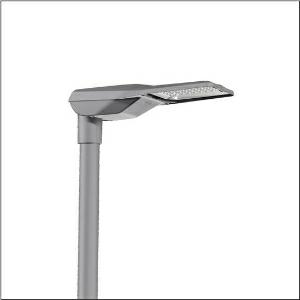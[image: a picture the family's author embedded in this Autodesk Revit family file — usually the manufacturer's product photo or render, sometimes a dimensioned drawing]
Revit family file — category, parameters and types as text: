
# Revit family: streetlight_sl_21_iq_mini___p0_8ab_5xe2r31g08hb_d767
name_source: partatom
category: Lighting Fixtures
units: mm (PartAtom-declared; Revit-internal decimal feet)

## family parameters
Cut with Voids When Loaded = No
Host = Face
Light Source = No
Part Type = Normal
Room Calculation Point = No
Round Connector Dimension = Use Diameter
Shared = No

## types (1)
- --- (1 x LED, 8210 lm, 70.9 W, 3000K)
    Apparent Load = 71 VA
    CIE Flux Codes = 36 71 98 100 100
    Color Rendering = 70
    Color Temperature = 3000K
    Default Elevation = 1800 mm
    Description = Streetlight SL 21 iQ mini, mast luminaire, primary light control with lens, of PMMA, primary optical cover: cover, of toughened safety glass, transparent, light distribution: P0.8aB, light emission: direct distribution, primary light characteristic: asymmetric, installation type: post-top, side-entry, LED, High Power LED, rated luminous flux: 8.210lm, luminous efficacy: 116lm/W, light colour: 730, colour temperature: 3000K, control gear: iQ Street-Remote, control: pre-setting: linear dimming characteristic, Street-Remote, Auto-Match, Temp-Guard, Lumen-Switch, Night-Set, Smart-Wire, Light-Fading, Desk-Remote (wireless, voltage-free reading and setting of iQ features in the workshop via application-optimized NFC function/RFID function), optimised constant luminous flux control (CLO 2.0), mains connection: 220..240V, AC, 50/60Hz, start of lifetime: 71W, end of service life: 75W, reduction: 31W, luminaire housing, of diecast aluminium, powder-coated, SITECO metallic grey (DB 702S), corrosivity category C5 high according to DIN EN ISO 12944, please order mast flange separately, inclination adjustable: 0°, 5°, 10°, 15°, sealing non-destructively replaceable, multi-level sealing system, length: 628mm, width: 235mm, height: 110mm, mast flange for spigot size: 42mm (side-entry): 5XC10008XM4, 60/48mm (side-entry/post-top): 5XC10108XM2, 76/60mm (side-entry/post-top): 5XC10108XM1, mounting height: 4..8m, protection rating (complete): IP66, insulation class (complete): insulation class II (safety insulation), certification: CE, ENEC, ENEC+, VDE, impact resistance: IK10, permissible operating ambient temperature for outdoor applications: -40..+50°C, standard-compliant lighting for roads and squares, packaging unit: 1 piece

Light Distribution: P0.8aB
    Height = 110 mm
    Lamp = 1 x LED
    Lamp Light Flux = 8210 lm
    Lamp Power = 70.9 W
    Lamp count = 1
    Length = 625 mm
    Luminous efficacy = 116 lm/W
    Manufacturer = Siteco
    ModVariant = No
    Model = 5XE2R31G08HB
    Number of Poles = 1
    OnlyDefault = Yes
    Power Factor = 1
    Product Name = Streetlight SL 21 iQ mini | P0.8aB
    Product group = mast luminaire | pylon top
    ProductGroupID = 6100
    Protection Class = Protection class II
    Protection Degree = IP 66
    RLX_Detail_Level = 1
    RLX_Emergency_Light_Flux = 0 lm
    RLX_Emergency_Type = 0
    RLX_Emergency_Type_DB = No
    RlxData = <blob elided: 91769 chars, md5=df5505a3>
    Socket = socket
    Standby Power = 0 W
    System Light Flux = 8210 lm
    System Power = 71 W
    Type Comments = factory setting: luminous flux: 100 % | dim-lin: 254 | 711 mA
    Type Image = l_1003519.jpg
    URL = http://relux.com
    VarID = @adj_082187
    Voltage = 0 V
    Weight = 0.00 kg
    Width = 234 mm

## geometry (parser evidence)
native form markers: Blend x4, Sweep x10
no freeform markers — native parametric forms only
